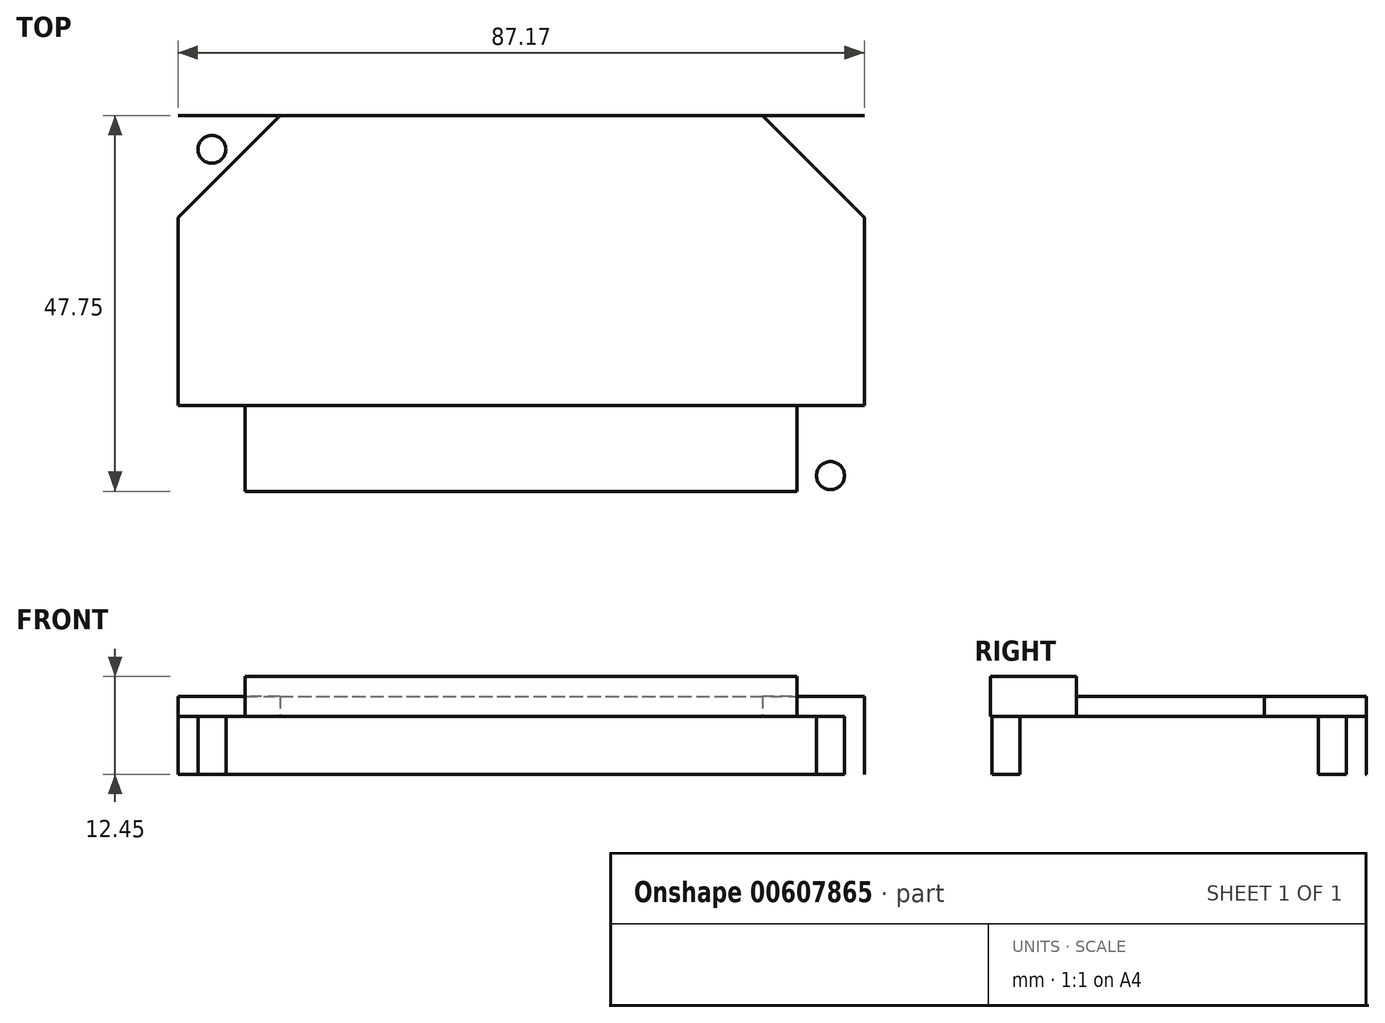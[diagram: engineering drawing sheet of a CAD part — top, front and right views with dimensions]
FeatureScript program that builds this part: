
annotation { "Feature Type Name" : "Feature", "Feature Type Description" : "" }
export const myFeature = defineFeature(function(context is Context, id is Id, definition is map)
    precondition{}
    {
        {
            var Q0;
            Q0=qCreatedBy(makeId("Top.planeOp"),FACE);
            var sketch = newSketch(context, id + "F0", { "sketchPlane" : qUnion([Q0])});
            skLineSegment(sketch, "E0.bottom", {"start": v(0, 0) * mm, "end": v(87.17, 0) * mm});
            skLineSegment(sketch, "E0.top", {"start": v(0, 50.04) * mm, "end": v(87.17, 50.04) * mm});
            skLineSegment(sketch, "E0.left", {"start": v(0, 0) * mm, "end": v(0, 50.04) * mm});
            skLineSegment(sketch, "E0.right", {"start": v(87.17, 0) * mm, "end": v(87.17, 50.04) * mm});
            skSolve(sketch);
        }
        {
            var Q0;
            Q0=makeQuery(id+"F0.imprint","IMPRINT",FACE,{"disambiguationData":[TD([[makeQuery(id+"F0.imprint","IMPRINT",EDGE,{"derivedFrom":sQuery(id+"F0.wireOp",EDGE,"E0.bottom")}),1.0]])]});
            extrude(context, id + "F1", {"entities" : qUnion([Q0]), "depth" : 7.37 * mm, "offsetDistance" : 25.4 * mm});
        }
        {
            var Q0;
            Q0=makeQuery(id+"F1.opExtrude","CAP_FACE",FACE,{"disambiguationData":[OSD([sQuery(id+"F0.wireOp",EDGE,"E0.bottom"),sQuery(id+"F0.wireOp",EDGE,"E0.top"),sQuery(id+"F0.wireOp",EDGE,"E0.left"),sQuery(id+"F0.wireOp",EDGE,"E0.right")])],"isStart":false});
            var sketch = newSketch(context, id + "F2", { "sketchPlane" : qUnion([Q0])});
            skLineSegment(sketch, "E1", {"start": v(0, 13.2) * mm, "end": v(87.17, 13.2) * mm});
            skLineSegment(sketch, "E2", {"start": v(87.17, 13.2) * mm, "end": v(87.17, 37.1) * mm});
            skLineSegment(sketch, "E3", {"start": v(87.17, 37.1) * mm, "end": v(74.24, 50.04) * mm});
            skLineSegment(sketch, "E4", {"start": v(74.24, 50.04) * mm, "end": v(12.93, 50.04) * mm});
            skLineSegment(sketch, "E5", {"start": v(12.93, 50.04) * mm, "end": v(0, 37.1) * mm});
            skLineSegment(sketch, "E6", {"start": v(0, 37.1) * mm, "end": v(0, 13.2) * mm});
            skSolve(sketch);
        }
        {
            var Q0;
            Q0=makeQuery(id+"F2.imprint","IMPRINT",FACE,{"disambiguationData":[TD([[makeQuery(id+"F2.imprint","IMPRINT",EDGE,{"derivedFrom":sQuery(id+"F2.wireOp",EDGE,"E1")}),1.0]])]});
            extrude(context, id + "F3", {"entities" : qUnion([Q0]), "operationType" : NewBodyOperationType.ADD, "depth" : 2.54 * mm, "offsetDistance" : 25.4 * mm});
        }
        {
            var Q0;
            {var subQ0=sQuery(id+"F0.wireOp",EDGE,"E0.left");var subQ1=sQuery(id+"F0.wireOp",EDGE,"E0.right");var subQ2=sQuery(id+"F0.wireOp",EDGE,"E0.bottom");Q0=makeQuery(id+"F3.boolean.opBoolean","SPLIT",FACE,{"disambiguationData":[TD([makeQuery(id+"F1.opExtrude","SWEPT_FACE",FACE,{"disambiguationData":[OSD([subQ2])]})])],"derivedFrom":makeQuery(id+"F1.opExtrude","CAP_FACE",FACE,{"disambiguationData":[OSD([subQ2,sQuery(id+"F0.wireOp",EDGE,"E0.top"),subQ0,subQ1])],"isStart":false})});}
            var sketch = newSketch(context, id + "F4", { "sketchPlane" : qUnion([Q0])});
            skLineSegment(sketch, "E7.bottom", {"start": v(8.53, 13.2) * mm, "end": v(78.64, 13.2) * mm});
            skLineSegment(sketch, "E7.top", {"start": v(8.53, 2.29) * mm, "end": v(78.64, 2.29) * mm});
            skLineSegment(sketch, "E7.left", {"start": v(8.53, 13.2) * mm, "end": v(8.53, 2.29) * mm});
            skLineSegment(sketch, "E7.right", {"start": v(78.64, 13.2) * mm, "end": v(78.64, 2.29) * mm});
            skLineSegment(sketch, "E8", {"start": v(8.53, 13.2) * mm, "end": v(0, 13.2) * mm});
            skLineSegment(sketch, "E9", {"start": v(78.64, 13.2) * mm, "end": v(87.17, 13.2) * mm});
            skSolve(sketch);
        }
        {
            var Q0;
            Q0=makeQuery(id+"F4.imprint","IMPRINT",FACE,{"disambiguationData":[TD([[makeQuery(id+"F4.imprint","IMPRINT",EDGE,{"derivedFrom":sQuery(id+"F4.wireOp",EDGE,"E7.bottom")}),-1.0]])]});
            extrude(context, id + "F5", {"entities" : qUnion([Q0]), "operationType" : NewBodyOperationType.ADD, "depth" : 5.08 * mm, "offsetDistance" : 25.4 * mm});
        }
        {
            var Q0;
            {var subQ0=sQuery(id+"F0.wireOp",EDGE,"E0.left");var subQ1=sQuery(id+"F0.wireOp",EDGE,"E0.right");var subQ2=sQuery(id+"F0.wireOp",EDGE,"E0.bottom");Q0=makeQuery(id+"F3.boolean.opBoolean","SPLIT",FACE,{"disambiguationData":[TD([makeQuery(id+"F1.opExtrude","SWEPT_FACE",FACE,{"disambiguationData":[OSD([subQ2])]})])],"derivedFrom":makeQuery(id+"F1.opExtrude","CAP_FACE",FACE,{"disambiguationData":[OSD([subQ2,sQuery(id+"F0.wireOp",EDGE,"E0.top"),subQ0,subQ1])],"isStart":false})});}
            var sketch = newSketch(context, id + "F6", { "sketchPlane" : qUnion([Q0])});
            skCircle(sketch, "E10", {"center": v(4.3, 4.3) * mm, "radius": 1.78 * mm});
            skLineSegment(sketch, "E11", {"start": v(4.3, 4.3) * mm, "end": v(0, 4.3) * mm, "construction": true});
            skLineSegment(sketch, "E12", {"start": v(4.3, 4.3) * mm, "end": v(4.3, 0) * mm, "construction": true});
            skLineSegment(sketch, "E13", {"start": v(43.59, 49.97) * mm, "end": v(43.59, 0) * mm, "construction": true});
            skLineSegment(sketch, "E14", {"start": v(0, 25.02) * mm, "end": v(87.37, 25.02) * mm, "construction": true});
            skLineSegment(sketch, "E15", {"start": v(0, 0) * mm, "end": v(0, 25.02) * mm});
            skPoint(sketch, "E16.0", {"position": v(6.47, 50.04) * mm});
            skLineSegment(sketch, "E17.0", {"start": v(0, 50.04) * mm, "end": v(12.93, 50.04) * mm});
            skLineSegment(sketch, "E18.0", {"start": v(74.24, 50.04) * mm, "end": v(87.17, 50.04) * mm});
            skLineSegment(sketch, "E19", {"start": v(0, 25.02) * mm, "end": v(0, 50.04) * mm});
            skLineSegment(sketch, "E20", {"start": v(0, 50.04) * mm, "end": v(43.59, 49.97) * mm});
            skLineSegment(sketch, "E21", {"start": v(87.17, 50.04) * mm, "end": v(87.37, 25.02) * mm});
            skLineSegment(sketch, "E22", {"start": v(87.37, 25.02) * mm, "end": v(87.17, 0) * mm});
            skLineSegment(sketch, "E23", {"start": v(87.17, 0) * mm, "end": v(43.59, 0) * mm});
            skLineSegment(sketch, "E24", {"start": v(43.59, 0) * mm, "end": v(0, 0) * mm});
            skLineSegment(sketch, "E25", {"start": v(43.59, 49.97) * mm, "end": v(87.17, 50.04) * mm});
            skCircle(sketch, "E26.MirrorC", {"center": v(82.88, 4.3) * mm, "radius": 1.78 * mm});
            skCircle(sketch, "E27.MirrorC", {"center": v(4.3, 45.75) * mm, "radius": 1.78 * mm});
            skCircle(sketch, "E28.MirrorC", {"center": v(82.88, 45.75) * mm, "radius": 1.78 * mm});
            skSolve(sketch);
        }
        {
            var Q0;
            Q0=makeQuery(id+"F6.imprint","IMPRINT",FACE,{"disambiguationData":[TD([[makeQuery(id+"F6.imprint","IMPRINT",EDGE,{"derivedFrom":sQuery(id+"F6.wireOp",EDGE,"E27.MirrorC")}),-1.0]])]});
            var Q1;
            Q1=makeQuery(id+"F6.imprint","IMPRINT",FACE,{"disambiguationData":[TD([[makeQuery(id+"F6.imprint","IMPRINT",EDGE,{"derivedFrom":sQuery(id+"F6.wireOp",EDGE,"E10")}),1.0]])]});
            var Q2;
            Q2=makeQuery(id+"F6.imprint","IMPRINT",FACE,{"disambiguationData":[TD([[makeQuery(id+"F6.imprint","IMPRINT",EDGE,{"derivedFrom":sQuery(id+"F6.wireOp",EDGE,"E26.MirrorC")}),-1.0]])]});
            var Q3;
            Q3=makeQuery(id+"F6.imprint","IMPRINT",FACE,{"disambiguationData":[TD([[makeQuery(id+"F6.imprint","IMPRINT",EDGE,{"derivedFrom":sQuery(id+"F6.wireOp",EDGE,"E28.MirrorC")}),1.0]])]});
            extrude(context, id + "F7", {"entities" : qUnion([Q0, Q1, Q2, Q3]), "operationType" : NewBodyOperationType.REMOVE, "endBound" : BoundingType.THROUGH_ALL, "oppositeDirection" : true, "depth" : 25.4 * mm, "offsetDistance" : 25.4 * mm});
        }
    });
